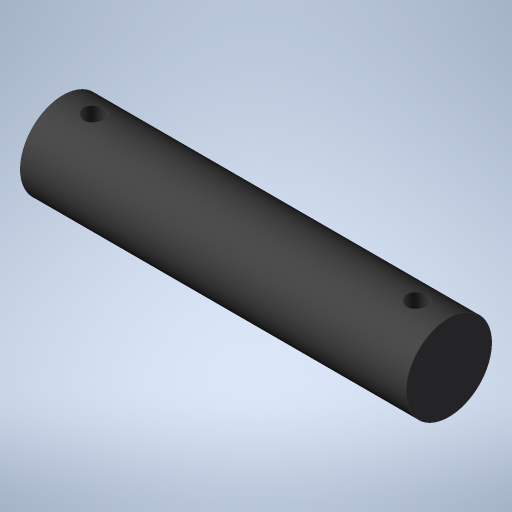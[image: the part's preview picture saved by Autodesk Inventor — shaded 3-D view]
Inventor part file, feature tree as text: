
AUTODESK INVENTOR PART (.ipt)
format: ipt  version: 2023 (Build 270158000, 158)  size: 238,080 bytes
history: native  units: in
note: dims shown in document units (in); Inventor stores cm internally (conversion verified against a paired STEP export)
features: extrude x2, sketch x2, plane x1
ambient origin geometry x8: Origin, YZ Plane, XZ Plane, XY Plane, X Axis, Y Axis, Z Axis, Center Point
bodies: Solid1 (feature_tree)
feature tree (5):
  extrude  "Extrusion1"  Depth=1.125in TaperAngle=0.0deg
  plane  "Work Plane1"
  extrude  "Extrusion2"  Depth=0.471in
  sketch  "Sketch1"  dims[d0=0.25in d1=1.125in d2=0.0in]
  sketch  "Sketch2"  dims[d3=0.1875in d4=0.471in d5=0.471in d6=0.06in d7=1.0in d8=0.0in]
